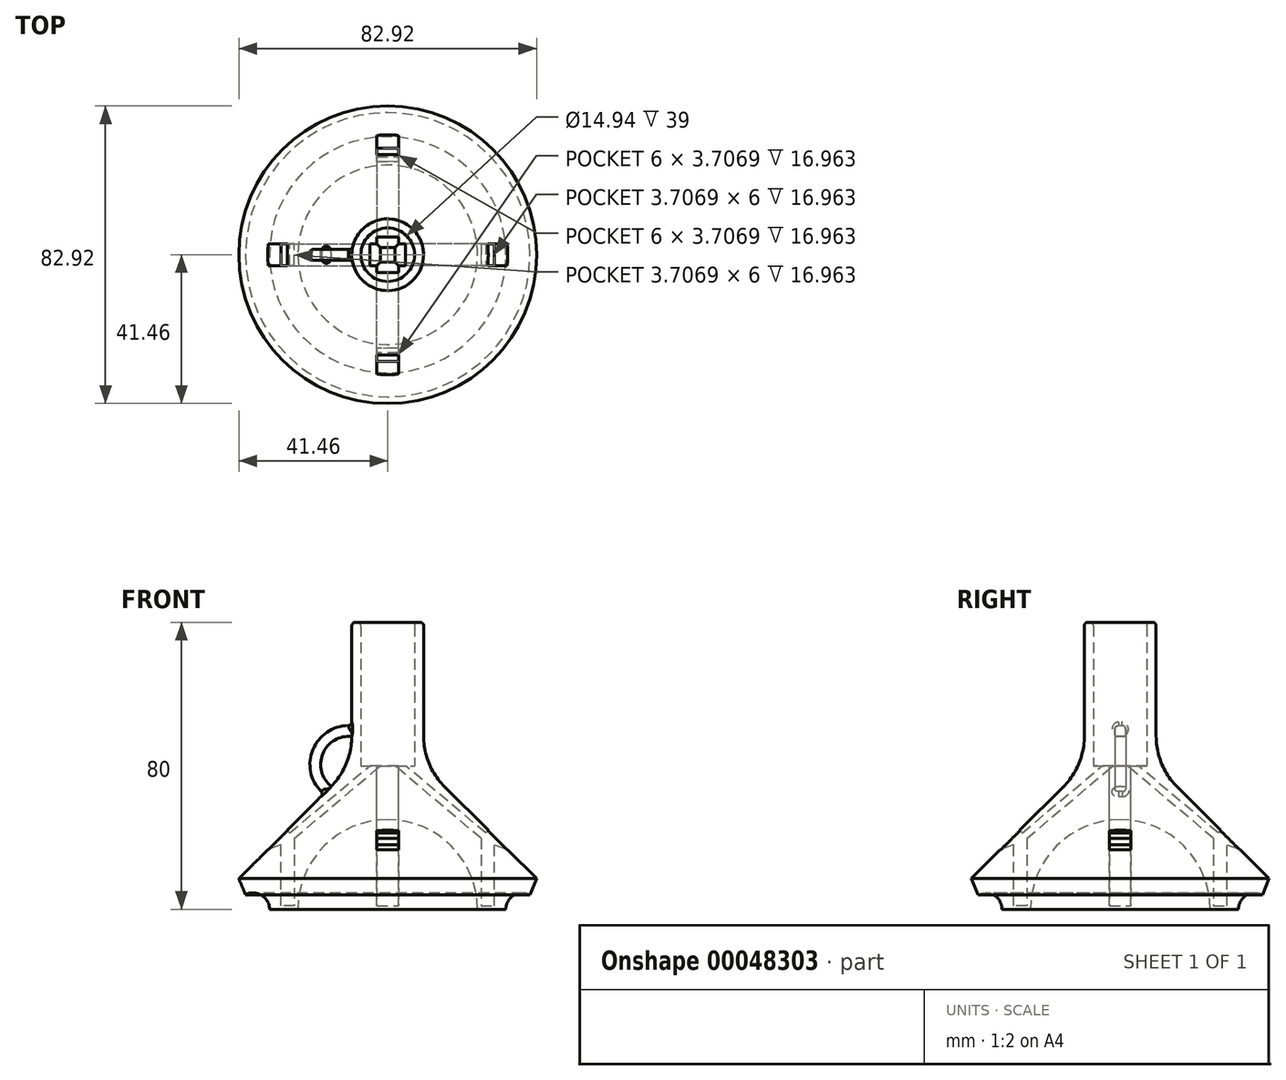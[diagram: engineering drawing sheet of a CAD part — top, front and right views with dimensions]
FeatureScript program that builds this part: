
annotation { "Feature Type Name" : "Feature", "Feature Type Description" : "" }
export const myFeature = defineFeature(function(context is Context, id is Id, definition is map)
    precondition{}
    {
        {
            var Q0;
            Q0=qCreatedBy(makeId("Front.planeOp"),FACE);
            var sketch = newSketch(context, id + "F0", { "sketchPlane" : qUnion([Q0])});
            skLineSegment(sketch, "E0", {"start": v(0, 0) * mm, "end": v(0, 80) * mm, "construction": true});
            skLineSegment(sketch, "E1", {"start": v(0, 80) * mm, "end": v(10, 80) * mm, "construction": true});
            skLineSegment(sketch, "E2", {"start": v(10, 80) * mm, "end": v(10, 40) * mm});
            skLineSegment(sketch, "E3", {"start": v(10, 40) * mm, "end": v(50, 0) * mm});
            skLineSegment(sketch, "E4", {"start": v(50, 0) * mm, "end": v(0, 0) * mm, "construction": true});
            skLineSegment(sketch, "E5", {"start": v(10, 80) * mm, "end": v(7.47, 80) * mm});
            skLineSegment(sketch, "E6", {"start": v(7.47, 80) * mm, "end": v(7.47, 40) * mm});
            skLineSegment(sketch, "E7", {"start": v(7.47, 40) * mm, "end": v(0, 40) * mm});
            skArc(sketch, "E8", {"start": v(25, 0) * mm, "mid": v(17.68, 17.68) * mm, "end": v(0, 25) * mm});
            skLineSegment(sketch, "E9", {"start": v(0, 40) * mm, "end": v(0, 25) * mm});
            skLineSegment(sketch, "E10", {"start": v(25, 0) * mm, "end": v(50, 0) * mm, "construction": true});
            skArc(sketch, "E11", {"start": v(42.08, 0) * mm, "mid": v(37.5, 4.58) * mm, "end": v(32.92, 0) * mm});
            skLineSegment(sketch, "E12", {"start": v(25, 0) * mm, "end": v(32.92, 0) * mm});
            skLineSegment(sketch, "E13", {"start": v(42.08, 0) * mm, "end": v(50, 0) * mm});
            skSolve(sketch);
        }
        {
            var Q0;
            Q0 = qSketchRegion(id + "F0", true);
            var Q1;
            Q1=sQuery(id+"F0.wireOp",EDGE,"E0");
            revolve(context, id + "F1", {"entities" : qUnion([Q0]), "axis" : qUnion([Q1]), "revolveType" : RevolveType.SYMMETRIC, "angle" : 90 * degree});
        }
        {
            var Q0;
            Q0=qCreatedBy(makeId("Front.planeOp"),FACE);
            var sketch = newSketch(context, id + "F2", { "sketchPlane" : qUnion([Q0])});
            skPoint(sketch, "E14.0", {"position": v(0, 40) * mm});
            skLineSegment(sketch, "E15", {"start": v(5.99, 44.01) * mm, "end": v(50, 0) * mm, "construction": true});
            skLineSegment(sketch, "E16", {"start": v(10, 80) * mm, "end": v(10, 40) * mm, "construction": true});
            skLineSegment(sketch, "E17", {"start": v(0, 40) * mm, "end": v(2, 40) * mm, "construction": true});
            skLineSegment(sketch, "E18", {"start": v(2, 40) * mm, "end": v(5, 40) * mm});
            skLineSegment(sketch, "E19", {"start": v(28, 22) * mm, "end": v(27.29, 21.3) * mm});
            skLineSegment(sketch, "E20", {"start": v(27.29, 21.3) * mm, "end": v(5, 40) * mm});
            skLineSegment(sketch, "E21", {"start": v(27.29, 21.3) * mm, "end": v(26, 19.77) * mm, "construction": true});
            skLineSegment(sketch, "E22", {"start": v(26, 19.77) * mm, "end": v(2, 40) * mm});
            skLineSegment(sketch, "E23", {"start": v(26.64, 20.53) * mm, "end": v(29.7, 17.96) * mm, "construction": true});
            skLineSegment(sketch, "E24", {"start": v(29.7, 17.96) * mm, "end": v(33.45, 16.55) * mm});
            skLineSegment(sketch, "E25", {"start": v(33.45, 16.55) * mm, "end": v(28, 22) * mm});
            skLineSegment(sketch, "E26", {"start": v(26, 19.77) * mm, "end": v(26, 0) * mm});
            skLineSegment(sketch, "E27", {"start": v(26, 0) * mm, "end": v(29.7, 0) * mm});
            skLineSegment(sketch, "E28", {"start": v(29.7, 0) * mm, "end": v(29.7, 17.96) * mm});
            skSolve(sketch);
        }
        {
            var Q0;
            Q0 = qSketchRegion(id + "F2", true);
            extrude(context, id + "F3", {"entities" : qUnion([Q0]), "operationType" : NewBodyOperationType.REMOVE, "endBound" : BoundingType.SYMMETRIC, "oppositeDirection" : true, "depth" : 6 * mm});
        }
        {
            var Q0;
            Q0=makeQuery(id+"F1.opRevolve","SWEPT_BODY",BODY,{"disambiguationData":[OSD([sQuery(id+"F0.wireOp",EDGE,"E2"),sQuery(id+"F0.wireOp",EDGE,"E3"),sQuery(id+"F0.wireOp",EDGE,"E5"),sQuery(id+"F0.wireOp",EDGE,"E6"),sQuery(id+"F0.wireOp",EDGE,"E7"),sQuery(id+"F0.wireOp",EDGE,"E8"),sQuery(id+"F0.wireOp",EDGE,"E9"),sQuery(id+"F0.wireOp",EDGE,"E11"),sQuery(id+"F0.wireOp",EDGE,"E12"),sQuery(id+"F0.wireOp",EDGE,"E13")])]});
            var Q1;
            Q1=makeQuery(id+"F1.opRevolve","CAP_EDGE",EDGE,{"disambiguationData":[OSD([sQuery(id+"F0.wireOp",EDGE,"E9")])],"isStart":true});
            circularPattern(context, id + "F4", {"operationType" : NewBodyOperationType.ADD, "entities" : qUnion([Q0]), "axis" : qUnion([Q1]), "angle" : 90 * degree, "instanceCount" : 4});
        }
        {
            var Q0;
            Q0=qCreatedBy(makeId("Top.planeOp"),FACE);
            var sketch = newSketch(context, id + "F5", { "sketchPlane" : qUnion([Q0])});
            skLineSegment(sketch, "E29.0", {"start": v(3, -29.7) * mm, "end": v(-3, -29.7) * mm});
            skLineSegment(sketch, "E30.0", {"start": v(-3, -26) * mm, "end": v(-3, -29.7) * mm});
            skLineSegment(sketch, "E31.0", {"start": v(3, -26) * mm, "end": v(-3, -26) * mm});
            skLineSegment(sketch, "E32.0", {"start": v(3, -26) * mm, "end": v(3, -29.7) * mm});
            skLineSegment(sketch, "E33.1.0", {"start": v(26, -3) * mm, "end": v(29.7, -3) * mm});
            skLineSegment(sketch, "E33.1.1", {"start": v(29.7, 3) * mm, "end": v(29.7, -3) * mm});
            skLineSegment(sketch, "E33.1.2", {"start": v(26, 3) * mm, "end": v(29.7, 3) * mm});
            skLineSegment(sketch, "E33.1.3", {"start": v(26, 3) * mm, "end": v(26, -3) * mm});
            skLineSegment(sketch, "E33.2.0", {"start": v(3, 26) * mm, "end": v(3, 29.7) * mm});
            skLineSegment(sketch, "E33.2.1", {"start": v(-3, 29.7) * mm, "end": v(3, 29.7) * mm});
            skLineSegment(sketch, "E33.2.2", {"start": v(-3, 26) * mm, "end": v(-3, 29.7) * mm});
            skLineSegment(sketch, "E33.2.3", {"start": v(-3, 26) * mm, "end": v(3, 26) * mm});
            skLineSegment(sketch, "E33.3.0", {"start": v(-26, 3) * mm, "end": v(-29.7, 3) * mm});
            skLineSegment(sketch, "E33.3.1", {"start": v(-29.7, -3) * mm, "end": v(-29.7, 3) * mm});
            skLineSegment(sketch, "E33.3.2", {"start": v(-26, -3) * mm, "end": v(-29.7, -3) * mm});
            skLineSegment(sketch, "E33.3.3", {"start": v(-26, -3) * mm, "end": v(-26, 3) * mm});
            skPoint(sketch, "E33.center", {"position": v(0, 0) * mm});
            skSolve(sketch);
        }
        {
            var Q0;
            Q0=makeQuery(id+"F5.imprint","IMPRINT",FACE,{"disambiguationData":[TD([[makeQuery(id+"F5.imprint","IMPRINT",EDGE,{"derivedFrom":sQuery(id+"F5.wireOp",EDGE,"E29.0")}),-1.0]])]});
            extrude(context, id + "F6", {"entities" : qUnion([Q0]), "operationType" : NewBodyOperationType.ADD, "depth" : 1 * mm});
        }
        {
            var Q0;
            Q0=makeQuery(id+"F5.imprint","IMPRINT",FACE,{"disambiguationData":[TD([[makeQuery(id+"F5.imprint","IMPRINT",EDGE,{"derivedFrom":sQuery(id+"F5.wireOp",EDGE,"E33.1.0")}),1.0]])]});
            extrude(context, id + "F7", {"entities" : qUnion([Q0]), "operationType" : NewBodyOperationType.ADD, "depth" : 1 * mm});
        }
        {
            var Q0;
            Q0=makeQuery(id+"F5.imprint","IMPRINT",FACE,{"disambiguationData":[TD([[makeQuery(id+"F5.imprint","IMPRINT",EDGE,{"derivedFrom":sQuery(id+"F5.wireOp",EDGE,"E33.2.0")}),1.0]])]});
            extrude(context, id + "F8", {"entities" : qUnion([Q0]), "operationType" : NewBodyOperationType.ADD, "depth" : 1 * mm});
        }
        {
            var Q0;
            Q0=makeQuery(id+"F5.imprint","IMPRINT",FACE,{"disambiguationData":[TD([[makeQuery(id+"F5.imprint","IMPRINT",EDGE,{"derivedFrom":sQuery(id+"F5.wireOp",EDGE,"E33.3.0")}),1.0]])]});
            extrude(context, id + "F9", {"entities" : qUnion([Q0]), "operationType" : NewBodyOperationType.ADD, "depth" : 1 * mm});
        }
        {
            var Q0;
            {var subQ0=makeQuery(id+"F1.opRevolve","SWEPT_FACE",FACE,{"disambiguationData":[OSD([sQuery(id+"F0.wireOp",EDGE,"E5")])]});Q0=makeQuery(id+"F4.boolean.opBoolean","MERGE",FACE,{"derivedFrom":[subQ0,makeQuery(id+"F4.opPattern","COPY",FACE,{"derivedFrom":subQ0,"instanceName":"1"}),makeQuery(id+"F4.opPattern","COPY",FACE,{"derivedFrom":subQ0,"instanceName":"2"}),makeQuery(id+"F4.opPattern","COPY",FACE,{"derivedFrom":subQ0,"instanceName":"3"})]});}
            fillet(context, id + "F10", {"entities" : qUnion([Q0]), "radius" : 1 * mm, "tangentPropagation" : true, "allowEdgeOverflow" : false});
        }
        {
            var Q0;
            {var subQ0=makeQuery(id+"F1.opRevolve","SWEPT_EDGE",EDGE,{"disambiguationData":[OSD([sQuery(id+"F0.wireOp",EDGE,"E2"),sQuery(id+"F0.wireOp",EDGE,"E3")])]});Q0=makeQuery(id+"F4.boolean.opBoolean","MERGE",EDGE,{"derivedFrom":[subQ0,makeQuery(id+"F4.opPattern","COPY",EDGE,{"derivedFrom":subQ0,"instanceName":"1"}),makeQuery(id+"F4.opPattern","COPY",EDGE,{"derivedFrom":subQ0,"instanceName":"2"}),makeQuery(id+"F4.opPattern","COPY",EDGE,{"derivedFrom":subQ0,"instanceName":"3"})]});}
            fillet(context, id + "F11", {"entities" : qUnion([Q0]), "radius" : 20 * mm, "tangentPropagation" : true, "allowEdgeOverflow" : false});
        }
        {
            var Q0;
            {var subQ0=makeQuery(id+"F1.opRevolve","SWEPT_EDGE",EDGE,{"disambiguationData":[OSD([sQuery(id+"F0.wireOp",EDGE,"E3"),sQuery(id+"F0.wireOp",EDGE,"E13")])]});Q0=makeQuery(id+"F4.boolean.opBoolean","MERGE",EDGE,{"derivedFrom":[subQ0,makeQuery(id+"F4.opPattern","COPY",EDGE,{"derivedFrom":subQ0,"instanceName":"1"}),makeQuery(id+"F4.opPattern","COPY",EDGE,{"derivedFrom":subQ0,"instanceName":"2"}),makeQuery(id+"F4.opPattern","COPY",EDGE,{"derivedFrom":subQ0,"instanceName":"3"})]});}
            chamfer(context, id + "F12", {"entities" : qUnion([Q0]), "width" : 5 * mm, "tangentPropagation" : true});
        }
        {
            var Q0;
            Q0=qCreatedBy(makeId("Front.planeOp"),FACE);
            var sketch = newSketch(context, id + "F13", { "sketchPlane" : qUnion([Q0])});
            skLineSegment(sketch, "E34", {"start": v(-10, 48.16) * mm, "end": v(-10, 79) * mm});
            skLineSegment(sketch, "E35", {"start": v(-46.46, 3.54) * mm, "end": v(-15.72, 34.28) * mm});
            skArc(sketch, "E36", {"start": v(-10, 48.16) * mm, "mid": v(-18.08, 43.37) * mm, "end": v(-15.72, 34.28) * mm});
            skArc(sketch, "E37.0", {"start": v(-9.71, 51.14) * mm, "mid": v(-20.88, 44.46) * mm, "end": v(-17.52, 31.88) * mm});
            skArc(sketch, "E38", {"start": v(-10, 48.16) * mm, "mid": v(-9.18, 49.59) * mm, "end": v(-9.71, 51.14) * mm});
            skArc(sketch, "E39", {"start": v(-17.52, 31.88) * mm, "mid": v(-16.08, 32.68) * mm, "end": v(-15.72, 34.28) * mm});
            skSolve(sketch);
        }
        {
            var Q0;
            Q0 = qSketchRegion(id + "F13", true);
            extrude(context, id + "F14", {"entities" : qUnion([Q0]), "operationType" : NewBodyOperationType.ADD, "endBound" : BoundingType.SYMMETRIC, "depth" : 3 * mm});
        }
        {
            var Q0;
            Q0=makeQuery(id+"F14.opExtrude","SWEPT_FACE",FACE,{"disambiguationData":[OSD([sQuery(id+"F13.wireOp",EDGE,"E37.0")])]});
            fillet(context, id + "F15", {"entities" : qUnion([Q0]), "radius" : 1 * mm, "tangentPropagation" : true, "allowEdgeOverflow" : false});
        }
    });
